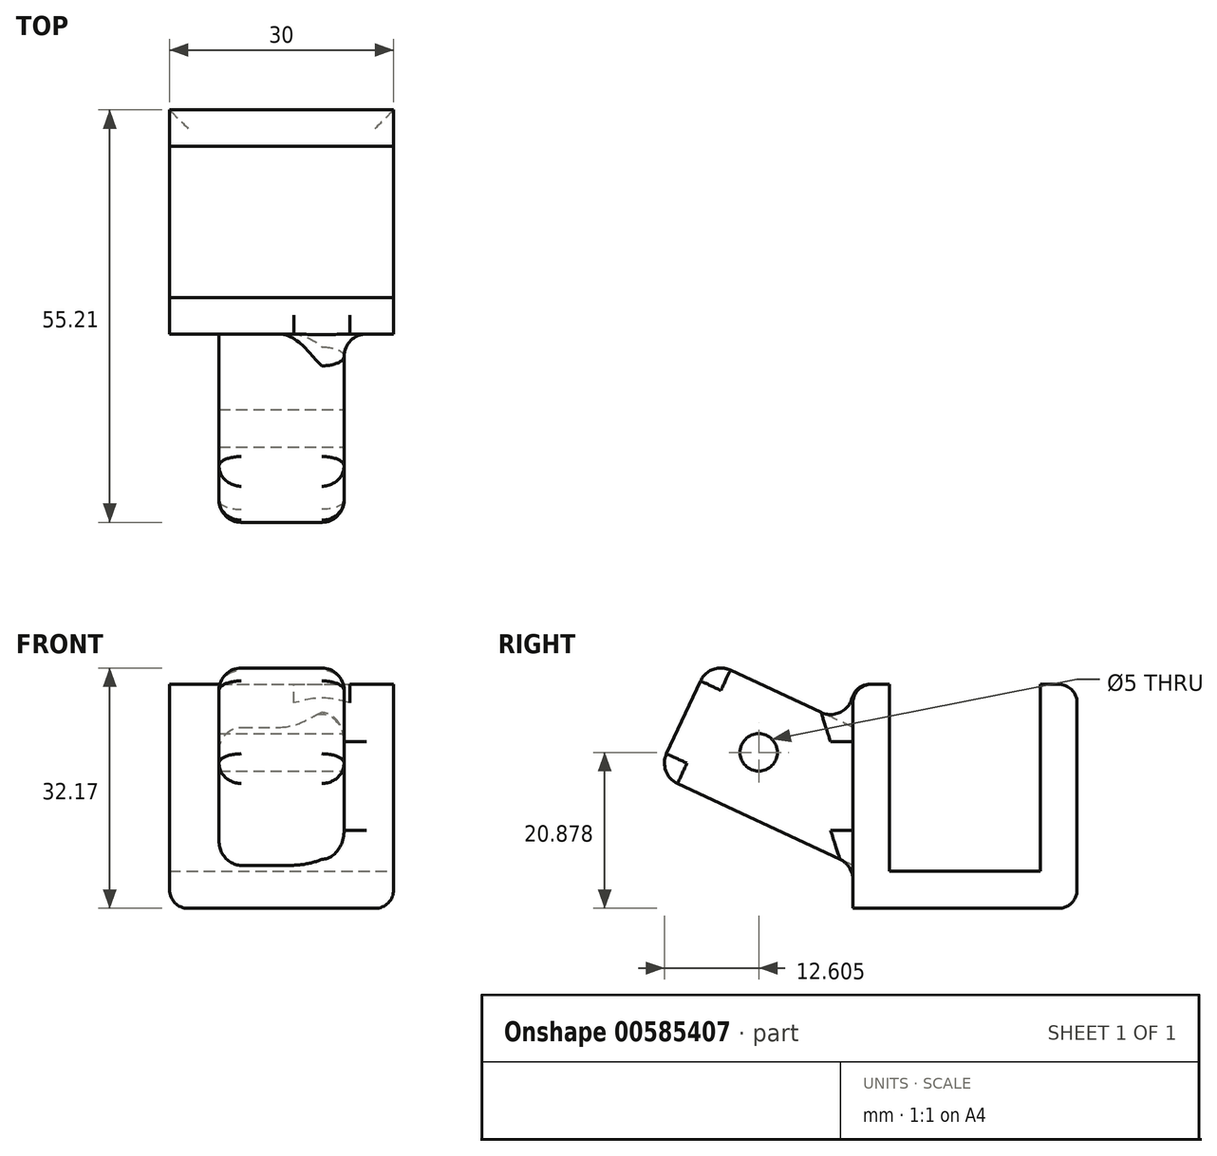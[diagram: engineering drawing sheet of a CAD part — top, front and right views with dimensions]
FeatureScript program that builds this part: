
annotation { "Feature Type Name" : "Feature", "Feature Type Description" : "" }
export const myFeature = defineFeature(function(context is Context, id is Id, definition is map)
    precondition{}
    {
        {
            var Q0;
            Q0=qCreatedBy(makeId("Top.planeOp"),FACE);
            var sketch = newSketch(context, id + "F0", { "sketchPlane" : qUnion([Q0])});
            skLineSegment(sketch, "E0.bottom", {"start": v(0, 0) * mm, "end": v(30, 0) * mm});
            skLineSegment(sketch, "E0.top", {"start": v(0, 30) * mm, "end": v(30, 30) * mm});
            skLineSegment(sketch, "E0.left", {"start": v(0, 0) * mm, "end": v(0, 30) * mm});
            skLineSegment(sketch, "E0.right", {"start": v(30, 0) * mm, "end": v(30, 30) * mm});
            skSolve(sketch);
        }
        {
            var Q0;
            Q0=makeQuery(id+"F0.imprint","IMPRINT",FACE,{"disambiguationData":[TD([[makeQuery(id+"F0.imprint","IMPRINT",EDGE,{"derivedFrom":sQuery(id+"F0.wireOp",EDGE,"E0.bottom")}),1.0]])]});
            extrude(context, id + "F1", {"entities" : qUnion([Q0]), "depth" : 5 * mm, "offsetDistance" : 25 * mm});
        }
        {
            var Q0;
            Q0=makeQuery(id+"F1.opExtrude","CAP_FACE",FACE,{"disambiguationData":[OSD([sQuery(id+"F0.wireOp",EDGE,"E0.bottom"),sQuery(id+"F0.wireOp",EDGE,"E0.top"),sQuery(id+"F0.wireOp",EDGE,"E0.left"),sQuery(id+"F0.wireOp",EDGE,"E0.right")])],"isStart":false});
            var sketch = newSketch(context, id + "F2", { "sketchPlane" : qUnion([Q0])});
            skLineSegment(sketch, "E1.bottom", {"start": v(0, 30) * mm, "end": v(30, 30) * mm});
            skLineSegment(sketch, "E1.top", {"start": v(0, 25.1) * mm, "end": v(30, 25.1) * mm});
            skLineSegment(sketch, "E1.left", {"start": v(0, 30) * mm, "end": v(0, 25.1) * mm});
            skLineSegment(sketch, "E1.right", {"start": v(30, 30) * mm, "end": v(30, 25.1) * mm});
            skLineSegment(sketch, "E2", {"start": v(0, 15) * mm, "end": v(30, 15) * mm, "construction": true});
            skLineSegment(sketch, "E3.MirrorCS", {"start": v(0, 0) * mm, "end": v(30, 0) * mm});
            skLineSegment(sketch, "E4.MirrorCS", {"start": v(0, 4.9) * mm, "end": v(30, 4.9) * mm});
            skLineSegment(sketch, "E5.MirrorCS", {"start": v(0, 0) * mm, "end": v(0, 4.9) * mm});
            skLineSegment(sketch, "E6.MirrorCS", {"start": v(30, 0) * mm, "end": v(30, 4.9) * mm});
            skSolve(sketch);
        }
        {
            var Q0;
            Q0=makeQuery(id+"F2.imprint","IMPRINT",FACE,{"disambiguationData":[TD([[makeQuery(id+"F2.imprint","IMPRINT",EDGE,{"derivedFrom":sQuery(id+"F2.wireOp",EDGE,"E1.bottom")}),-1.0]])]});
            var Q1;
            Q1=makeQuery(id+"F2.imprint","IMPRINT",FACE,{"disambiguationData":[TD([[makeQuery(id+"F2.imprint","IMPRINT",EDGE,{"derivedFrom":sQuery(id+"F2.wireOp",EDGE,"E3.MirrorCS")}),1.0]])]});
            extrude(context, id + "F3", {"entities" : qUnion([Q0, Q1]), "operationType" : NewBodyOperationType.ADD, "depth" : 25 * mm, "offsetDistance" : 25 * mm});
        }
        {
            var Q0;
            Q0=makeQuery(id+"F3.boolean.opBoolean","MERGE",FACE,{"derivedFrom":[makeQuery(id+"F1.opExtrude","SWEPT_FACE",FACE,{"disambiguationData":[OSD([sQuery(id+"F0.wireOp",EDGE,"E0.bottom")])]}),makeQuery(id+"F3.opExtrude","SWEPT_FACE",FACE,{"disambiguationData":[OSD([sQuery(id+"F2.wireOp",EDGE,"E3.MirrorCS")])]})]});
            var sketch = newSketch(context, id + "F4", { "sketchPlane" : qUnion([Q0])});
            skLineSegment(sketch, "E7", {"start": v(0, 30) * mm, "end": v(30, 0) * mm, "construction": true});
            skLineSegment(sketch, "E8", {"start": v(30, 30) * mm, "end": v(0, 0) * mm, "construction": true});
            skLineSegment(sketch, "E9", {"start": v(30, 15) * mm, "end": v(0, 15) * mm, "construction": true});
            skPoint(sketch, "E10", {"position": v(15, 15) * mm});
            skSolve(sketch);
        }
        {
            var Q0;
            Q0=sQuery(id+"F4.wireOp",EDGE,"E9");
            cPlane(context, id + "F5", {"entities" : qUnion([Q0]), "cplaneType" : CPlaneType.LINE_ANGLE, "offset" : 25 * mm, "angle" : 25 * degree, "width" : 150 * mm, "height" : 150 * mm});
        }
        {
            var Q0;
            Q0=qCreatedBy(id+"F5.planeOp",FACE);
            var sketch = newSketch(context, id + "F6", { "sketchPlane" : qUnion([Q0])});
            skLineSegment(sketch, "E11", {"start": v(15, -12.68) * mm, "end": v(15, 27.19) * mm, "construction": true});
            skLineSegment(sketch, "E12.right", {"start": v(23.38, 5.22) * mm, "end": v(23.38, 21.97) * mm});
            skLineSegment(sketch, "E13.MirrorCS", {"start": v(6.63, 5.22) * mm, "end": v(6.63, 21.97) * mm});
            skLineSegment(sketch, "E14", {"start": v(6.63, 21.97) * mm, "end": v(23.38, 21.97) * mm});
            skLineSegment(sketch, "E15", {"start": v(6.63, 5.22) * mm, "end": v(23.38, 5.22) * mm});
            skLineSegment(sketch, "E16", {"start": v(6.63, 21.97) * mm, "end": v(23.38, 5.22) * mm, "construction": true});
            skLineSegment(sketch, "E17", {"start": v(23.38, 21.97) * mm, "end": v(6.63, 5.22) * mm, "construction": true});
            skPoint(sketch, "E18", {"position": v(15, 13.6) * mm});
            skSolve(sketch);
        }
        {
            var Q0;
            Q0=makeQuery(id+"F6.imprint","IMPRINT",FACE,{"disambiguationData":[TD([[makeQuery(id+"F6.imprint","IMPRINT",EDGE,{"derivedFrom":sQuery(id+"F6.wireOp",EDGE,"E12.right")}),1.0]])]});
            extrude(context, id + "F7", {"entities" : qUnion([Q0]), "operationType" : NewBodyOperationType.ADD, "depth" : 25 * mm, "offsetDistance" : 25 * mm});
        }
        {
            var Q0;
            Q0=makeQuery(id+"F7.opExtrude","CAP_FACE",FACE,{"disambiguationData":[OSD([sQuery(id+"F6.wireOp",EDGE,"E12.right"),sQuery(id+"F6.wireOp",EDGE,"E13.MirrorCS"),sQuery(id+"F6.wireOp",EDGE,"E14"),sQuery(id+"F6.wireOp",EDGE,"E15")])],"isStart":true});
            extrude(context, id + "F8", {"entities" : qUnion([Q0]), "operationType" : NewBodyOperationType.ADD, "endBound" : BoundingType.UP_TO_NEXT, "depth" : 25 * mm, "offsetDistance" : 25 * mm});
        }
        {
            var Q0;
            Q0=makeQuery(id+"F7.opExtrude","CAP_EDGE",EDGE,{"disambiguationData":[OSD([sQuery(id+"F6.wireOp",EDGE,"E12.top"),sQuery(id+"F6.wireOp",EDGE,"2b287bc2-b91f-4d5c-92d6-7b527b62b60b0.MirrorCS")])],"isStart":true});
            var Q1;
            Q1=makeQuery(id+"F7.opExtrude","CAP_EDGE",EDGE,{"disambiguationData":[OSD([sQuery(id+"F6.wireOp",EDGE,"E12.top"),sQuery(id+"F6.wireOp",EDGE,"2b287bc2-b91f-4d5c-92d6-7b527b62b60b0.MirrorCS")])],"isStart":false});
            var Q2;
            Q2=makeQuery(id+"F7.opExtrude","CAP_EDGE",EDGE,{"disambiguationData":[OSD([sQuery(id+"F6.wireOp",EDGE,"E13.MirrorCS")])],"isStart":false});
            var Q3;
            Q3=makeQuery(id+"F7.opExtrude","SWEPT_EDGE",EDGE,{"disambiguationData":[OSD([sQuery(id+"F6.wireOp",EDGE,"2b287bc2-b91f-4d5c-92d6-7b527b62b60b0.MirrorCS"),sQuery(id+"F6.wireOp",EDGE,"E13.MirrorCS")])]});
            var Q4;
            Q4=makeQuery(id+"F7.opExtrude","SWEPT_EDGE",EDGE,{"disambiguationData":[OSD([sQuery(id+"F0.wireOp",EDGE,"E0.bottom"),sQuery(id+"F6.wireOp",EDGE,"6c4bcf0f-9b09-45c1-b559-46fb84961e650.MirrorCS"),sQuery(id+"F6.wireOp",EDGE,"E13.MirrorCS")])]});
            var Q5;
            Q5=makeQuery(id+"F7.opExtrude","CAP_EDGE",EDGE,{"disambiguationData":[OSD([sQuery(id+"F6.wireOp",EDGE,"E12.right")])],"isStart":true});
            var Q6;
            Q6=makeQuery(id+"F7.opExtrude","SWEPT_FACE",FACE,{"disambiguationData":[OSD([sQuery(id+"F6.wireOp",EDGE,"E12.right")])]});
            var Q7;
            Q7=makeQuery(id+"F7.opExtrude","CAP_EDGE",EDGE,{"disambiguationData":[OSD([sQuery(id+"F6.wireOp",EDGE,"E12.bottom"),sQuery(id+"F6.wireOp",EDGE,"6c4bcf0f-9b09-45c1-b559-46fb84961e650.MirrorCS")])],"isStart":false});
            fillet(context, id + "F9", {"entities" : qUnion([Q0, Q1, Q2, Q3, Q4, Q5, Q6, Q7]), "radius" : 3 * mm, "tangentPropagation" : true, "allowEdgeOverflow" : false});
        }
        {
            var Q0;
            Q0=makeQuery(id+"F3.opExtrude","CAP_EDGE",EDGE,{"disambiguationData":[OSD([sQuery(id+"F2.wireOp",EDGE,"E1.bottom")])],"isStart":false});
            var Q1;
            Q1=makeQuery(id+"F3.opExtrude","CAP_EDGE",EDGE,{"disambiguationData":[OSD([sQuery(id+"F2.wireOp",EDGE,"E3.MirrorCS")])],"isStart":false});
            var Q2;
            Q2=makeQuery(id+"F1.opExtrude","CAP_EDGE",EDGE,{"disambiguationData":[OSD([sQuery(id+"F0.wireOp",EDGE,"E0.top")])],"isStart":true});
            var Q3;
            Q3=makeQuery(id+"F1.opExtrude","CAP_EDGE",EDGE,{"disambiguationData":[OSD([sQuery(id+"F0.wireOp",EDGE,"E0.right")])],"isStart":true});
            var Q4;
            Q4=makeQuery(id+"F1.opExtrude","CAP_EDGE",EDGE,{"disambiguationData":[OSD([sQuery(id+"F0.wireOp",EDGE,"E0.left")])],"isStart":true});
            fillet(context, id + "F10", {"entities" : qUnion([Q0, Q1, Q2, Q3, Q4]), "radius" : 2.5 * mm, "tangentPropagation" : true, "allowEdgeOverflow" : false});
        }
        {
            var Q0;
            Q0=makeQuery(id+"F7.opExtrude","CAP_EDGE",EDGE,{"disambiguationData":[OSD([sQuery(id+"F6.wireOp",EDGE,"E15")])],"isStart":false});
            var Q1;
            Q1=makeQuery(id+"F7.opExtrude","CAP_EDGE",EDGE,{"disambiguationData":[OSD([sQuery(id+"F6.wireOp",EDGE,"E14")])],"isStart":false});
            fillet(context, id + "F11", {"entities" : qUnion([Q0, Q1]), "radius" : 3 * mm, "tangentPropagation" : true, "allowEdgeOverflow" : false});
        }
        {
            var Q0;
            Q0=makeQuery(id+"F7.opExtrude","SWEPT_FACE",FACE,{"disambiguationData":[OSD([sQuery(id+"F6.wireOp",EDGE,"E12.right")])]});
            var sketch = newSketch(context, id + "F12", { "sketchPlane" : qUnion([Q0])});
            skCircle(sketch, "E19", {"center": v(-12.6, 20.88) * mm, "radius": 2.5 * mm});
            skLineSegment(sketch, "E20", {"start": v(-3, 22.33) * mm, "end": v(-7.54, 12.59) * mm, "construction": true});
            skLineSegment(sketch, "E21", {"start": v(-7.54, 12.59) * mm, "end": v(-17.67, 29.17) * mm, "construction": true});
            skLineSegment(sketch, "E22", {"start": v(-22.21, 19.43) * mm, "end": v(-3, 22.33) * mm, "construction": true});
            skSolve(sketch);
        }
        {
            var Q0;
            Q0=makeQuery(id+"F12.imprint","IMPRINT",FACE,{"disambiguationData":[TD([[makeQuery(id+"F12.imprint","IMPRINT",EDGE,{"derivedFrom":sQuery(id+"F12.wireOp",EDGE,"E19")}),1.0]])]});
            extrude(context, id + "F13", {"entities" : qUnion([Q0]), "operationType" : NewBodyOperationType.REMOVE, "endBound" : BoundingType.UP_TO_NEXT, "oppositeDirection" : true, "depth" : 25 * mm, "offsetDistance" : 25 * mm});
        }
    });
